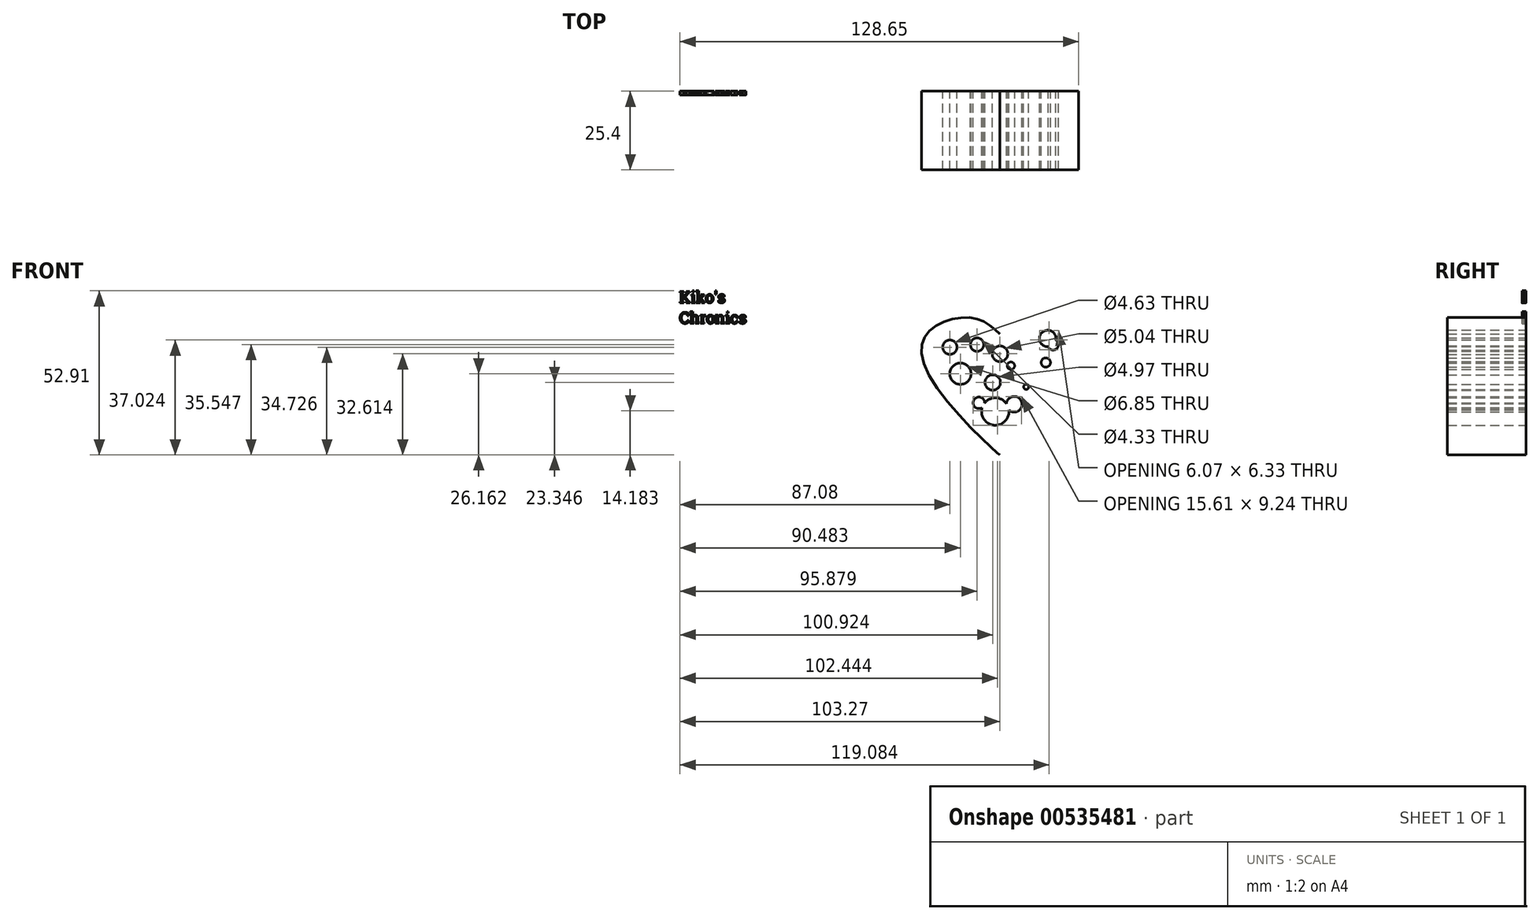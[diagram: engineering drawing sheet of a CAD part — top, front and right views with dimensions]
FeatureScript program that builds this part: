
annotation { "Feature Type Name" : "Feature", "Feature Type Description" : "" }
export const myFeature = defineFeature(function(context is Context, id is Id, definition is map)
    precondition{}
    {
        {
            var Q0;
            Q0=qCreatedBy(makeId("Front.planeOp"),FACE);
            var sketch = newSketch(context, id + "F0", { "sketchPlane" : qUnion([Q0])});
            skFitSpline(sketch, "E0", {"points": [v(0, 42) * mm, v(7.98, 47.04) * mm, v(21.7, 44) * mm, v(23.46, 29.8) * mm, v(0, 3.05) * mm, v(0, 3.17) * mm], "startDerivative": vector(37.62, 35.4) * mm, "endDerivative": vector(2.74, 8.43) * mm});
            skFitSpline(sketch, "E1.MirrorCS", {"points": [v(0, 42) * mm, v(-7.98, 47.04) * mm, v(-21.7, 44) * mm, v(-23.46, 29.8) * mm, v(0, 3.05) * mm, v(0, 3.17) * mm], "startDerivative": vector(-37.62, 35.4) * mm, "endDerivative": vector(-2.74, 8.43) * mm});
            skSolve(sketch);
        }
        {
            var Q0;
            Q0=qCreatedBy(makeId("Front.planeOp"),FACE);
            var sketch = newSketch(context, id + "F1", { "sketchPlane" : qUnion([Q0])});
            skCircle(sketch, "E2", {"center": v(-16.19, 37.78) * mm, "radius": 2.31 * mm});
            skCircle(sketch, "E3", {"center": v(-12.79, 29.21) * mm, "radius": 3.43 * mm});
            skCircle(sketch, "E4", {"center": v(-6.8, 19.83) * mm, "radius": 1.85 * mm});
            skCircle(sketch, "E5", {"center": v(0, 35.66) * mm, "radius": 2.52 * mm});
            skCircle(sketch, "E6", {"center": v(-2.35, 26.4) * mm, "radius": 2.49 * mm});
            skCircle(sketch, "E7", {"center": v(8.45, 24.99) * mm, "radius": 0.83 * mm});
            skCircle(sketch, "E8", {"center": v(14.78, 32.85) * mm, "radius": 1.5 * mm});
            skCircle(sketch, "E9", {"center": v(15.37, 40.6) * mm, "radius": 2.66 * mm});
            skCircle(sketch, "E10", {"center": v(17.13, 38.6) * mm, "radius": 1.73 * mm});
            skCircle(sketch, "E11", {"center": v(4.58, 19.36) * mm, "radius": 2.52 * mm});
            skCircle(sketch, "E12", {"center": v(-1.53, 17.01) * mm, "radius": 4.42 * mm});
            skCircle(sketch, "E13", {"center": v(3.52, 31.8) * mm, "radius": 1.2 * mm});
            skCircle(sketch, "E14", {"center": v(-7.4, 38.6) * mm, "radius": 2.16 * mm});
            skSolve(sketch);
        }
        {
            var Q0;
            Q0 = qSketchRegion(id + "F0", true);
            extrude(context, id + "F2", {"entities" : qUnion([Q0]), "depth" : 25.4 * mm, "offsetDistance" : 25.4 * mm});
        }
        {
            var Q0;
            Q0 = qSketchRegion(id + "F1", true);
            extrude(context, id + "F3", {"entities" : qUnion([Q0]), "depth" : 25.4 * mm, "offsetDistance" : 25.4 * mm});
        }
        {
            var Q0;
            Q0=makeQuery(id+"F3.opExtrude","SWEPT_BODY",BODY,{"disambiguationData":[OSD([sQuery(id+"F1.wireOp",EDGE,"E2")])]});
            var Q1;
            Q1=makeQuery(id+"F3.opExtrude","SWEPT_BODY",BODY,{"disambiguationData":[OSD([sQuery(id+"F1.wireOp",EDGE,"E4"),sQuery(id+"F1.wireOp",EDGE,"E11"),sQuery(id+"F1.wireOp",EDGE,"E12")])]});
            var Q2;
            Q2=makeQuery(id+"F3.opExtrude","SWEPT_BODY",BODY,{"disambiguationData":[OSD([sQuery(id+"F1.wireOp",EDGE,"E6")])]});
            var Q3;
            Q3=makeQuery(id+"F3.opExtrude","SWEPT_BODY",BODY,{"disambiguationData":[OSD([sQuery(id+"F1.wireOp",EDGE,"E8")])]});
            var Q4;
            Q4=makeQuery(id+"F3.opExtrude","SWEPT_BODY",BODY,{"disambiguationData":[OSD([sQuery(id+"F1.wireOp",EDGE,"E13")])]});
            var Q5;
            Q5=makeQuery(id+"F3.opExtrude","SWEPT_BODY",BODY,{"disambiguationData":[OSD([sQuery(id+"F1.wireOp",EDGE,"E3")])]});
            var Q6;
            Q6=makeQuery(id+"F3.opExtrude","SWEPT_BODY",BODY,{"disambiguationData":[OSD([sQuery(id+"F1.wireOp",EDGE,"E7")])]});
            var Q7;
            Q7=makeQuery(id+"F3.opExtrude","SWEPT_BODY",BODY,{"disambiguationData":[OSD([sQuery(id+"F1.wireOp",EDGE,"E14")])]});
            var Q8;
            Q8=makeQuery(id+"F3.opExtrude","SWEPT_BODY",BODY,{"disambiguationData":[OSD([sQuery(id+"F1.wireOp",EDGE,"E9"),sQuery(id+"F1.wireOp",EDGE,"E10")])]});
            var Q9;
            Q9=makeQuery(id+"F3.opExtrude","SWEPT_BODY",BODY,{"disambiguationData":[OSD([sQuery(id+"F1.wireOp",EDGE,"E5")])]});
            var Q10;
            Q10=makeQuery(id+"F2.opExtrude","SWEPT_BODY",BODY,{"disambiguationData":[OSD([sQuery(id+"F0.wireOp",EDGE,"E0"),sQuery(id+"F0.wireOp",EDGE,"E1.MirrorCS")])]});
            booleanBodies(context, id + "F4", {"operationType" : BooleanOperationType.SUBTRACTION, "tools" : qUnion([Q0, Q1, Q2, Q3, Q4, Q5, Q6, Q7, Q8, Q9]), "targets" : qUnion([Q10])});
        }
        {
            var Q0;
            Q0=qCreatedBy(makeId("Front.planeOp"),FACE);
            var sketch = newSketch(context, id + "F5", { "sketchPlane" : qUnion([Q0])});
            skText(sketch, "E15", { "text": "Kiko\'s\nChronics", "fontName": "RobotoSlab-Regular.ttf"});
            const initialGuessF5  = {"E15": [-0.10345, 0.05211, 1, 0, 0.00364]};
            skSetInitialGuess(sketch, initialGuessF5);
            skSolve(sketch);
        }
        {
            var Q0;
            Q0 = qSketchRegion(id + "F5", true);
            extrude(context, id + "F6", {"entities" : qUnion([Q0]), "depth" : 1.27 * mm, "offsetDistance" : 25.4 * mm});
        }
    });
